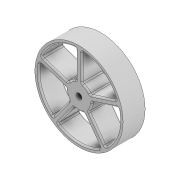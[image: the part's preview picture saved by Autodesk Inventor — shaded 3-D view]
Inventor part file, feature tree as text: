
AUTODESK INVENTOR PART (.ipt)
format: ipt  version: 2020 (Build 240168000, 168)  size: 296,960 bytes
history: native  units: mm
features: other x1, extrude x1, fillet x1, sketch x1
ambient origin geometry x8: Origin, YZ Plane, XZ Plane, XY Plane, X Axis, Y Axis, Z Axis, Center Point
bodies: Body1 (feature_tree)
feature tree (4):
  other  "솔리드1"
  extrude  "돌출1"  Depth=50.0mm TaperAngle=360.0deg
  fillet  "모깎기1"  Radius=120.0mm
  sketch  "스케치1"
